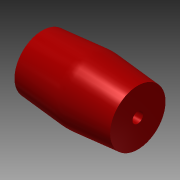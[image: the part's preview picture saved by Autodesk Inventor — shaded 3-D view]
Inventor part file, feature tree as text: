
AUTODESK INVENTOR PART (.ipt)
format: ipt  version: 2014 SP2 (Build 180246200, 246)  size: 103,424 bytes
history: native  units: mm
features: sketch x5, extrude x2, chamfer x2, fillet x1, projected_geometry x1
ambient origin geometry x8: Origin, YZ Plane, XZ Plane, XY Plane, X Axis, Y Axis, Z Axis, Center Point
bodies: Solid1 (feature_tree)
feature tree (11):
  sketch  "Sketch1"  dims[d1=18.0mm d2=0.0mm d4=18.0mm d5=0.0mm]
  sketch  "Sketch2"  dims[d6=9.0mm d7=2.0mm d8=0.872665mm d9=9.0mm d10=2.0mm d11=0.872665mm]
  extrude  "Extrusion1"  Depth=18.0mm TaperAngle=0.0deg
  sketch  "Sketch4"
  extrude  "Extrusion2"  Depth=9.0mm
  chamfer  "Chamfer1"  [1 undecoded]
  chamfer  "Chamfer2"  [1 undecoded]
  fillet  "Fillet1"  [1 undecoded]
  sketch  "Sketch3"  dims[d12=10.0mm]
  projected_geometry  "Projected Loop1"
  sketch  "Sketch5"
note: 3 required parameter values undecoded (feature->parameter linkage not recoverable at this tier; creation-order binding heuristic only, values carry confidence <= 0.55)
